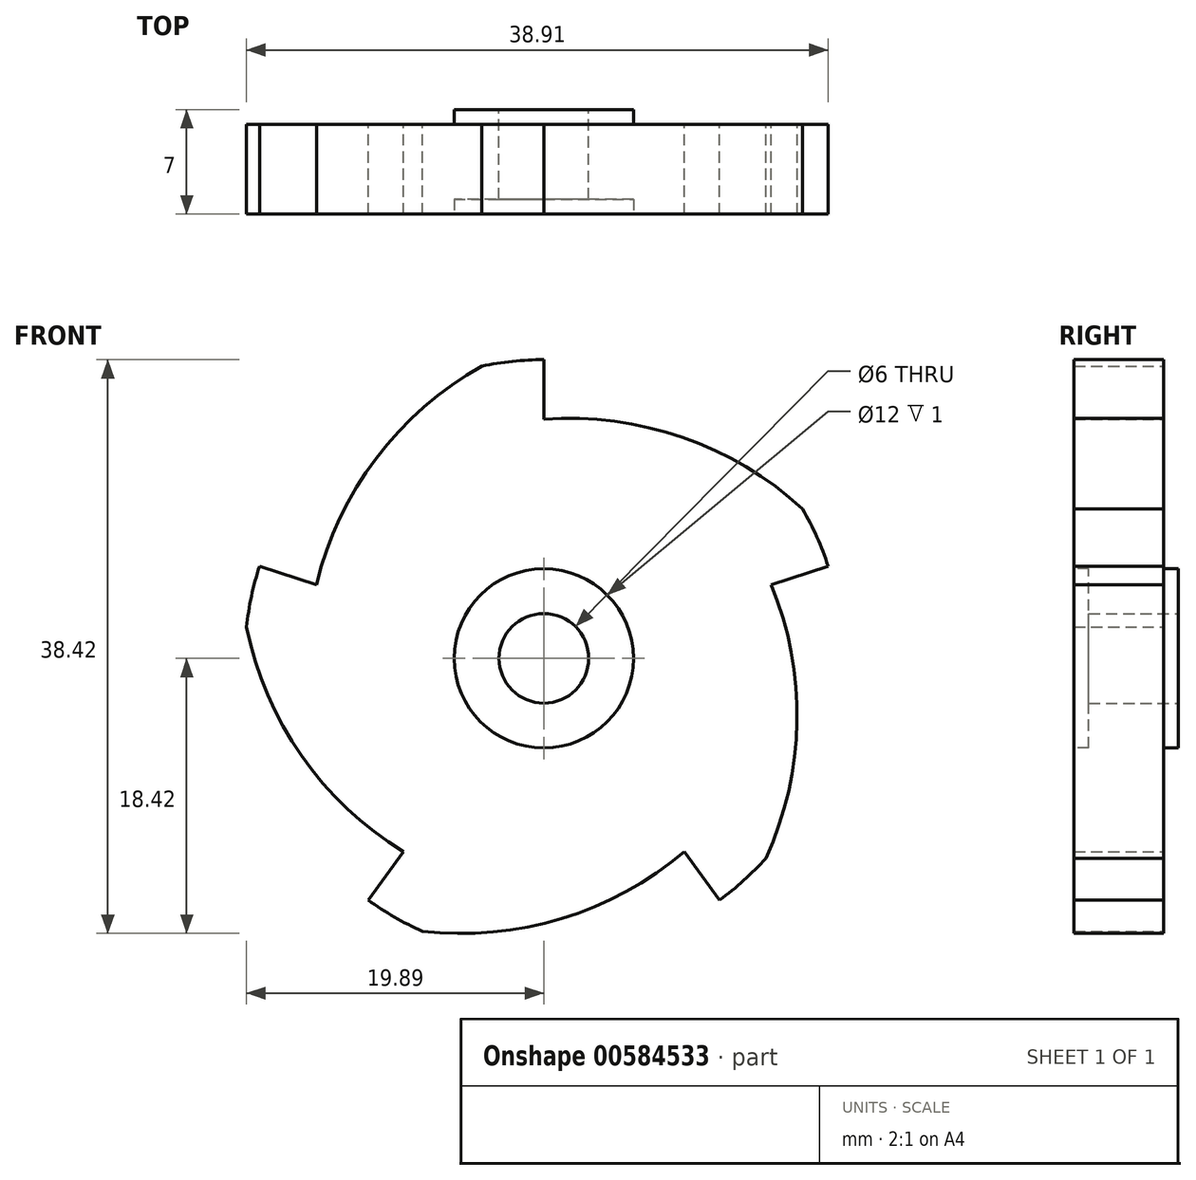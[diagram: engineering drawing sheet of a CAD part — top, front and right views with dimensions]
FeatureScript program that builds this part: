
annotation { "Feature Type Name" : "Feature", "Feature Type Description" : "" }
export const myFeature = defineFeature(function(context is Context, id is Id, definition is map)
    precondition{}
    {
        {
            var Q0;
            Q0=qCreatedBy(makeId("Front.planeOp"),FACE);
            var sketch = newSketch(context, id + "F0", { "sketchPlane" : qUnion([Q0])});
            skArc(sketch, "E0", {"start": v(0, 20) * mm, "mid": v(-10, -17.32) * mm, "end": v(17.32, 10) * mm});
            skArc(sketch, "E1", {"start": v(17.32, 10) * mm, "mid": v(9.28, 14.8) * mm, "end": v(0, 16) * mm});
            skLineSegment(sketch, "E2", {"start": v(0, 16) * mm, "end": v(0, 20) * mm});
            skLineSegment(sketch, "E3", {"start": v(0, 0) * mm, "end": v(17.32, 10) * mm});
            skCircle(sketch, "E4", {"center": v(0, 0) * mm, "radius": 3 * mm});
            skSolve(sketch);
        }
        {
            var Q0;
            Q0=makeQuery(id+"F0.imprint","IMPRINT",FACE,{"disambiguationData":[TD([[makeQuery(id+"F0.imprint","IMPRINT",EDGE,{"derivedFrom":sQuery(id+"F0.wireOp",EDGE,"E0")}),1.0]])]});
            extrude(context, id + "F1", {"entities" : qUnion([Q0]), "depth" : 6 * mm, "offsetDistance" : 25 * mm});
        }
        {
            var Q0;
            Q0=makeQuery(id+"F1.opExtrude","CAP_FACE",FACE,{"disambiguationData":[OSD([sQuery(id+"F0.wireOp",EDGE,"E0"),sQuery(id+"F0.wireOp",EDGE,"E1"),sQuery(id+"F0.wireOp",EDGE,"E2"),sQuery(id+"F0.wireOp",EDGE,"E4")])],"isStart":true});
            var sketch = newSketch(context, id + "F2", { "sketchPlane" : qUnion([Q0])});
            skCircle(sketch, "E5", {"center": v(0, 0) * mm, "radius": 6 * mm});
            skSolve(sketch);
        }
        {
            var Q0;
            Q0=makeQuery(id+"F2.imprint","IMPRINT",FACE,{"disambiguationData":[TD([[makeQuery(id+"F2.imprint","IMPRINT",EDGE,{"derivedFrom":sQuery(id+"F2.wireOp",EDGE,"E5")}),1.0]])]});
            extrude(context, id + "F3", {"entities" : qUnion([Q0]), "operationType" : NewBodyOperationType.ADD, "depth" : 1 * mm, "offsetDistance" : 25 * mm});
        }
        {
            var Q0;
            Q0=makeQuery(id+"F1.opExtrude","CAP_FACE",FACE,{"disambiguationData":[OSD([sQuery(id+"F0.wireOp",EDGE,"E0"),sQuery(id+"F0.wireOp",EDGE,"E1"),sQuery(id+"F0.wireOp",EDGE,"E2"),sQuery(id+"F0.wireOp",EDGE,"E4")])],"isStart":false});
            var sketch = newSketch(context, id + "F4", { "sketchPlane" : qUnion([Q0])});
            skCircle(sketch, "E6", {"center": v(0, 0) * mm, "radius": 6 * mm});
            skSolve(sketch);
        }
        {
            var Q0;
            Q0=makeQuery(id+"F4.imprint","IMPRINT",FACE,{"disambiguationData":[TD([[makeQuery(id+"F4.imprint","IMPRINT",EDGE,{"derivedFrom":sQuery(id+"F4.wireOp",EDGE,"E6")}),1.0]])]});
            extrude(context, id + "F5", {"entities" : qUnion([Q0]), "operationType" : NewBodyOperationType.REMOVE, "oppositeDirection" : true, "depth" : 1 * mm, "offsetDistance" : 25 * mm});
        }
        {
            var Q0;
            Q0=makeQuery(id+"F1.opExtrude","SWEPT_FACE",FACE,{"disambiguationData":[OSD([sQuery(id+"F0.wireOp",EDGE,"E1")])]});
            var Q1;
            Q1=makeQuery(id+"F1.opExtrude","SWEPT_FACE",FACE,{"disambiguationData":[OSD([sQuery(id+"F0.wireOp",EDGE,"E2")])]});
            var Q2;
            {var subQ0=sQuery(id+"F0.wireOp",EDGE,"E4");Q2=makeQuery(id+"F3.boolean.opBoolean","MERGE",FACE,{"derivedFrom":[makeQuery(id+"F1.opExtrude","SWEPT_FACE",FACE,{"disambiguationData":[OSD([subQ0])]}),makeQuery(id+"F3.opExtrude","SWEPT_FACE",FACE,{"disambiguationData":[OSD([subQ0])]})]});}
            circularPattern(context, id + "F6", {"patternType" : PatternType.FACE, "faces" : qUnion([Q0, Q1]), "axis" : qUnion([Q2]), "angle" : 360 * degree, "instanceCount" : 5, "equalSpace" : true});
        }
    });
